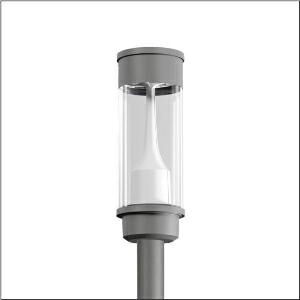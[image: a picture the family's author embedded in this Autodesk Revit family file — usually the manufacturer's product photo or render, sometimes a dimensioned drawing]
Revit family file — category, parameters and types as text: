
# Revit family: litepole_iq___p1_0a_5xa5415bf14h_51c2
name_source: partatom
category: Lighting Fixtures
units: mm (PartAtom-declared; Revit-internal decimal feet)

## family parameters
Cut with Voids When Loaded = No
Host = Face
Light Source = No
Part Type = Normal
Room Calculation Point = No
Round Connector Dimension = Use Diameter
Shared = No

## types (1)
- --- (1 x LED, 1510 lm, 12.9 W, 2200K)
    Apparent Load = 13 VA
    CIE Flux Codes = 32 61 90 93 100
    Color Rendering = 70
    Color Temperature = 2200K
    Default Elevation = 1800 mm
    Description = Litepole iQ, mast luminaire, Module 540 iQ-SR, primary light control with 3 zone facetted reflector, of plastic, silver coated, highly specular, structured, primary optical cover: cover, of PMMA, transparent, partly coated, light distribution: P1.0a, light emission: direct distribution, primary light characteristic: strongly asymmetric, installation type: post-top, LED, High Power LED, rated luminous flux: 1.510lm, luminous efficacy: 117lm/W, light colour: 722, colour temperature: 2200K, control gear: ECG iQ, control: optimised constant luminous flux control (CLO 2.0), Desk-Remote (wireless, voltage-free reading and setting of iQ features in the workshop via application-optimized NFC function/RFID function), Light-Fading, Smart-Wire, Night-Set, Lumen-Switch, Temp-Guard, Auto-Match, Street-Remote, presetting dimming logarithmic, with terminal, 6-pole, max. 2.5mm², mains connection: 230..240V, AC, 50/60Hz, start of lifetime: 13W, end of service life: 13W, reduction: 6W, luminaire housing, upper part, of glass-fibre reinforced polyester, coated, Siteco® metallic grey (DB 702S), diameter: 210mm, height: 590mm, spigot size: d x l = 76 x 70mm (post-top) | with reducer (optional accessory) 60 x 70mm, post-top mast mounting element, of diecast aluminium, coated, Siteco® metallic grey (DB 702S), Module 540 iQ-SR, traffic white (RAL 9016), equipment: standard, protection rating (complete): IP65, insulation class (complete): insulation class II (safety insulation), certification: CE, ENEC, VDE, packaging unit: 1 piece

Light Distribution: P1.0a
    Height = 590 mm
    Lamp = 1 x LED
    Lamp Light Flux = 1510 lm
    Lamp Power = 12.9 W
    Lamp count = 1
    Length = 220 mm
    Luminous efficacy = 117 lm/W
    Manufacturer = Siteco
    ModVariant = No
    Model = 5XA5415BF14H
    Number of Poles = 1
    OnlyDefault = Yes
    Power Factor = 1
    Product Name = Litepole iQ | P1.0a
    Product group = mast luminaire | pylon top
    ProductGroupID = 6100
    Protection Class = Protection class II
    Protection Degree = IP 65
    RLX_Detail_Level = 1
    RLX_Emergency_Light_Flux = 0 lm
    RLX_Emergency_Type = 0
    RLX_Emergency_Type_DB = No
    RlxData = <blob elided: 64309 chars, md5=ee7aace0>
    Socket = socket
    Standby Power = 0 W
    System Light Flux = 1510 lm
    System Power = 13 W
    Type Comments = factory setting: luminous flux: 100 % | dim-lin: 254 | 516 mA
    Type Image = l_1006025.jpg
    URL = http://relux.com
    VarID = @adj_108937
    Voltage = 0 V
    Weight = 0.00 kg
    Width = 0 mm  [stored 0 ft]

note: [stored X ft] marks values corroborated as IEEE doubles in the binary element streams (Revit-internal decimal feet)

## geometry (parser evidence)
native form markers: Blend x4, Sweep x14
no freeform markers — native parametric forms only
